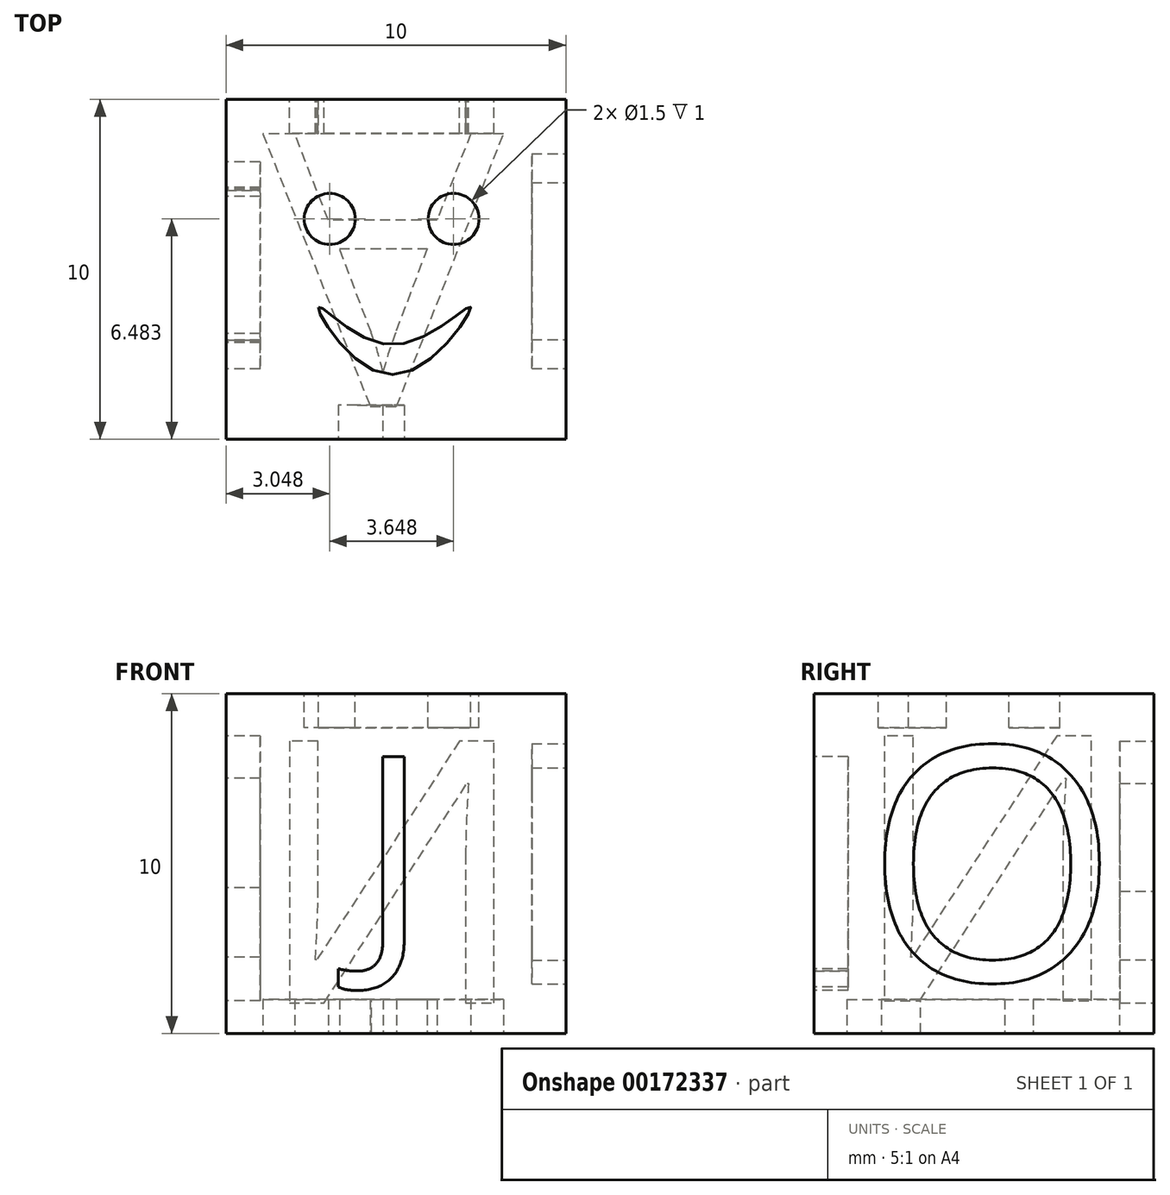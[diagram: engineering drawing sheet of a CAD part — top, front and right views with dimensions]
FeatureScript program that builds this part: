
annotation { "Feature Type Name" : "Feature", "Feature Type Description" : "" }
export const myFeature = defineFeature(function(context is Context, id is Id, definition is map)
    precondition{}
    {
        {
            var Q0;
            Q0=qCreatedBy(makeId("Front.planeOp"),FACE);
            var sketch = newSketch(context, id + "F0", { "sketchPlane" : qUnion([Q0])});
            skLineSegment(sketch, "E0.bottom", {"start": v(0, 0) * mm, "end": v(10, 0) * mm});
            skLineSegment(sketch, "E0.top", {"start": v(0, -10) * mm, "end": v(10, -10) * mm});
            skLineSegment(sketch, "E0.left", {"start": v(0, 0) * mm, "end": v(0, -10) * mm});
            skLineSegment(sketch, "E0.right", {"start": v(10, 0) * mm, "end": v(10, -10) * mm});
            skSolve(sketch);
        }
        {
            var Q0;
            Q0 = qSketchRegion(id + "F0", true);
            extrude(context, id + "F1", {"entities" : qUnion([Q0]), "depth" : 10 * mm});
        }
        {
            var Q0;
            Q0=makeQuery(id+"F1.opExtrude","CAP_FACE",FACE,{"disambiguationData":[OSD([sQuery(id+"F0.wireOp",EDGE,"E0.bottom"),sQuery(id+"F0.wireOp",EDGE,"E0.top"),sQuery(id+"F0.wireOp",EDGE,"E0.left"),sQuery(id+"F0.wireOp",EDGE,"E0.right")])],"isStart":false});
            var sketch = newSketch(context, id + "F2", { "sketchPlane" : qUnion([Q0])});
            skText(sketch, "E1", { "text": "J", "fontName": "OpenSans-Regular.ttf"});
            const initialGuessF2  = {"E1": [0.0039, -0.0073, 1, 0, 0.0055]};
            skSetInitialGuess(sketch, initialGuessF2);
            skSolve(sketch);
        }
        {
            var Q0;
            Q0 = qSketchRegion(id + "F2", true);
            extrude(context, id + "F3", {"entities" : qUnion([Q0]), "operationType" : NewBodyOperationType.REMOVE, "oppositeDirection" : true, "depth" : 1 * mm});
        }
        {
            var Q0;
            Q0=makeQuery(id+"F1.opExtrude","SWEPT_FACE",FACE,{"disambiguationData":[OSD([sQuery(id+"F0.wireOp",EDGE,"E0.right")])]});
            var sketch = newSketch(context, id + "F4", { "sketchPlane" : qUnion([Q0])});
            skText(sketch, "E2", { "text": "O", "fontName": "OpenSans-Regular.ttf"});
            const initialGuessF4  = {"E2": [-0.00851, -0.00845, 1, 0, 0.00693]};
            skSetInitialGuess(sketch, initialGuessF4);
            skSolve(sketch);
        }
        {
            var Q0;
            Q0 = qSketchRegion(id + "F4", true);
            extrude(context, id + "F5", {"entities" : qUnion([Q0]), "operationType" : NewBodyOperationType.REMOVE, "oppositeDirection" : true, "depth" : 1 * mm});
        }
        {
            var Q0;
            Q0=makeQuery(id+"F1.opExtrude","CAP_FACE",FACE,{"disambiguationData":[OSD([sQuery(id+"F0.wireOp",EDGE,"E0.bottom"),sQuery(id+"F0.wireOp",EDGE,"E0.top"),sQuery(id+"F0.wireOp",EDGE,"E0.left"),sQuery(id+"F0.wireOp",EDGE,"E0.right")])],"isStart":true});
            var sketch = newSketch(context, id + "F6", { "sketchPlane" : qUnion([Q0])});
            skText(sketch, "E3", { "text": "N", "fontName": "OpenSans-Regular.ttf"});
            const initialGuessF6  = {"E3": [-0.00894, -0.0091, 1, 0, 0.00777]};
            skSetInitialGuess(sketch, initialGuessF6);
            skSolve(sketch);
        }
        {
            var Q0;
            Q0 = qSketchRegion(id + "F6", true);
            extrude(context, id + "F7", {"entities" : qUnion([Q0]), "operationType" : NewBodyOperationType.REMOVE, "oppositeDirection" : true, "depth" : 1 * mm});
        }
        {
            var Q0;
            Q0=makeQuery(id+"F1.opExtrude","SWEPT_FACE",FACE,{"disambiguationData":[OSD([sQuery(id+"F0.wireOp",EDGE,"E0.left")])]});
            var sketch = newSketch(context, id + "F8", { "sketchPlane" : qUnion([Q0])});
            skText(sketch, "E4", { "text": "N", "fontName": "OpenSans-Regular.ttf"});
            const initialGuessF8  = {"E4": [0.00076, -0.00904, 1, 0, 0.00787]};
            skSetInitialGuess(sketch, initialGuessF8);
            skSolve(sketch);
        }
        {
            var Q0;
            Q0 = qSketchRegion(id + "F8", true);
            extrude(context, id + "F9", {"entities" : qUnion([Q0]), "operationType" : NewBodyOperationType.REMOVE, "oppositeDirection" : true, "depth" : 1 * mm});
        }
        {
            var Q0;
            Q0=makeQuery(id+"F1.opExtrude","SWEPT_FACE",FACE,{"disambiguationData":[OSD([sQuery(id+"F0.wireOp",EDGE,"E0.top")])]});
            var sketch = newSketch(context, id + "F10", { "sketchPlane" : qUnion([Q0])});
            skText(sketch, "E5", { "text": "A", "fontName": "OpenSans-Regular.ttf"});
            const initialGuessF10  = {"E5": [0.00108, 0.00101, 1, 0, 0.00806]};
            skSetInitialGuess(sketch, initialGuessF10);
            skSolve(sketch);
        }
        {
            var Q0;
            Q0 = qSketchRegion(id + "F10", true);
            extrude(context, id + "F11", {"entities" : qUnion([Q0]), "operationType" : NewBodyOperationType.REMOVE, "oppositeDirection" : true, "depth" : 1 * mm});
        }
        {
            var Q0;
            Q0=makeQuery(id+"F1.opExtrude","SWEPT_FACE",FACE,{"disambiguationData":[OSD([sQuery(id+"F0.wireOp",EDGE,"E0.bottom")])]});
            var sketch = newSketch(context, id + "F12", { "sketchPlane" : qUnion([Q0])});
            skCircle(sketch, "E6", {"center": v(3.05, -3.52) * mm, "radius": 0.75 * mm});
            skCircle(sketch, "E7", {"center": v(6.7, -3.52) * mm, "radius": 0.75 * mm});
            skFitSpline(sketch, "E8", {"points": [v(2.72, -6.11) * mm, v(4.87, -7.22) * mm, v(7.2, -6.11) * mm, v(4.87, -8.1) * mm, v(2.72, -6.11) * mm]});
            skSolve(sketch);
        }
        {
            var Q0;
            Q0 = qSketchRegion(id + "F12", true);
            extrude(context, id + "F13", {"entities" : qUnion([Q0]), "operationType" : NewBodyOperationType.REMOVE, "oppositeDirection" : true, "depth" : 1 * mm});
        }
    });
